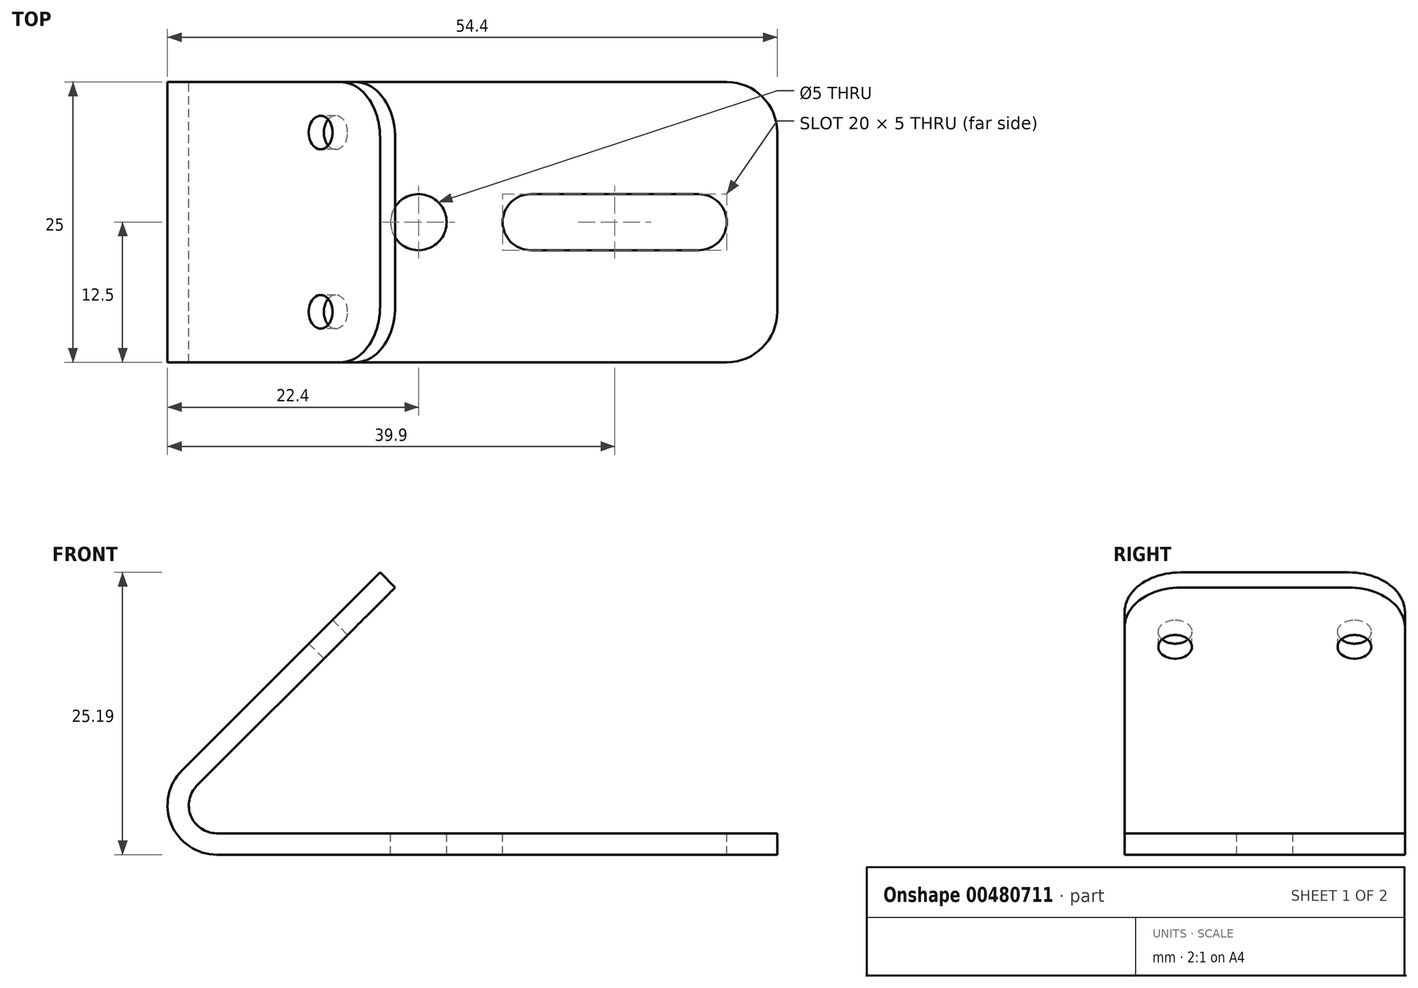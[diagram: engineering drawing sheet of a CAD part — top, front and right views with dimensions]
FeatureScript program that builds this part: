
annotation { "Feature Type Name" : "Feature", "Feature Type Description" : "" }
export const myFeature = defineFeature(function(context is Context, id is Id, definition is map)
    precondition{}
    {
        {
            var Q0;
            Q0=qCreatedBy(makeId("Front.planeOp"),FACE);
            var sketch = newSketch(context, id + "F0", { "sketchPlane" : qUnion([Q0])});
            skLineSegment(sketch, "E0", {"start": v(0, 0) * mm, "end": v(-50, 0) * mm});
            skLineSegment(sketch, "E1", {"start": v(-53.11, 7.51) * mm, "end": v(-35.43, 25.19) * mm});
            skPoint(sketch, "E2.visualSharp", {"position": v(-60.62, 0) * mm});
            skArc(sketch, "E2.filletArc", {"start": v(-53.11, 7.51) * mm, "mid": v(-54.07, 2.72) * mm, "end": v(-50, 0) * mm});
            skLineSegment(sketch, "E3.0", {"start": v(-51.77, 6.17) * mm, "end": v(-34.1, 23.85) * mm});
            skArc(sketch, "E3.1", {"start": v(-51.77, 6.17) * mm, "mid": v(-52.3, 3.44) * mm, "end": v(-50, 1.9) * mm});
            skLineSegment(sketch, "E3.2", {"start": v(0, 1.9) * mm, "end": v(-50, 1.9) * mm});
            skLineSegment(sketch, "E4", {"start": v(-35.43, 25.19) * mm, "end": v(-34.1, 23.85) * mm});
            skLineSegment(sketch, "E5", {"start": v(0, 1.9) * mm, "end": v(0, 0) * mm});
            skSolve(sketch);
        }
        {
            var Q0;
            Q0 = qSketchRegion(id + "F0", true);
            extrude(context, id + "F1", {"entities" : qUnion([Q0]), "endBound" : BoundingType.SYMMETRIC, "depth" : 25 * mm});
        }
        {
            var Q0;
            Q0=makeQuery(id+"F1.opExtrude","SWEPT_FACE",FACE,{"disambiguationData":[OSD([sQuery(id+"F0.wireOp",EDGE,"E3.2")])]});
            var sketch = newSketch(context, id + "F2", { "sketchPlane" : qUnion([Q0])});
            skCircle(sketch, "E6", {"center": v(-32, 0) * mm, "radius": 2.5 * mm});
            skLineSegment(sketch, "E7.0", {"start": v(-4.5, 12.5) * mm, "end": v(-50, 12.5) * mm});
            skLineSegment(sketch, "E8.0", {"start": v(0, -8) * mm, "end": v(0, 8) * mm});
            skLineSegment(sketch, "E9.0", {"start": v(-4.5, -12.5) * mm, "end": v(-50, -12.5) * mm});
            skPoint(sketch, "E10.visualSharp", {"position": v(0, 12.5) * mm});
            skArc(sketch, "E10.filletArc", {"start": v(0, 8) * mm, "mid": v(-1.32, 11.18) * mm, "end": v(-4.5, 12.5) * mm});
            skPoint(sketch, "E11.visualSharp", {"position": v(0, -12.5) * mm});
            skArc(sketch, "E11.filletArc", {"start": v(-4.5, -12.5) * mm, "mid": v(-1.32, -11.18) * mm, "end": v(0, -8) * mm});
            skLineSegment(sketch, "E12.bottom", {"start": v(-22, 2.5) * mm, "end": v(-7, 2.5) * mm});
            skLineSegment(sketch, "E12.top", {"start": v(-22, -2.5) * mm, "end": v(-7, -2.5) * mm});
            skPoint(sketch, "E12.middle", {"position": v(-14.5, 0) * mm});
            skArc(sketch, "E13", {"start": v(-22, 2.5) * mm, "mid": v(-24.5, 0) * mm, "end": v(-22, -2.5) * mm});
            skArc(sketch, "E14", {"start": v(-7, 2.5) * mm, "mid": v(-4.5, 0) * mm, "end": v(-7, -2.5) * mm});
            skSolve(sketch);
        }
        {
            var Q0;
            Q0=makeQuery(id+"F2.imprint","IMPRINT",FACE,{"disambiguationData":[TD([[makeQuery(id+"F2.imprint","IMPRINT",EDGE,{"derivedFrom":sQuery(id+"F2.wireOp",EDGE,"E6")}),1.0]])]});
            var Q1;
            {var subQ0=sQuery(id+"F2.wireOp",EDGE,"E10.filletArc");Q1=makeQuery(id+"F2.imprint","IMPRINT",FACE,{"disambiguationData":[TD([[makeQuery(id+"F2.imprint","IMPRINT",EDGE,{"derivedFrom":subQ0}),-1.0]])]});}
            var Q2;
            {var subQ0=sQuery(id+"F2.wireOp",EDGE,"E11.filletArc");Q2=makeQuery(id+"F2.imprint","IMPRINT",FACE,{"disambiguationData":[TD([[makeQuery(id+"F2.imprint","IMPRINT",EDGE,{"derivedFrom":subQ0}),-1.0]])]});}
            var Q3;
            Q3=makeQuery(id+"F2.imprint","IMPRINT",FACE,{"disambiguationData":[TD([[makeQuery(id+"F2.imprint","IMPRINT",EDGE,{"derivedFrom":sQuery(id+"F2.wireOp",EDGE,"E12.bottom")}),-1.0]])]});
            extrude(context, id + "F3", {"entities" : qUnion([Q0, Q1, Q2, Q3]), "operationType" : NewBodyOperationType.REMOVE, "endBound" : BoundingType.THROUGH_ALL, "oppositeDirection" : true, "depth" : 25 * mm});
        }
        {
            var Q0;
            Q0=makeQuery(id+"F1.opExtrude","SWEPT_FACE",FACE,{"disambiguationData":[OSD([sQuery(id+"F0.wireOp",EDGE,"E1")])]});
            var sketch = newSketch(context, id + "F4", { "sketchPlane" : qUnion([Q0])});
            skCircle(sketch, "E15", {"center": v(-8, -14.74) * mm, "radius": 1.5 * mm});
            skCircle(sketch, "E16", {"center": v(8, -14.74) * mm, "radius": 1.5 * mm});
            skLineSegment(sketch, "E17.0", {"start": v(12.5, -32.24) * mm, "end": v(12.5, -12.24) * mm});
            skLineSegment(sketch, "E18.0", {"start": v(-12.5, -32.24) * mm, "end": v(-12.5, -12.24) * mm});
            skLineSegment(sketch, "E19.0", {"start": v(7.5, -7.24) * mm, "end": v(-7.5, -7.24) * mm});
            skPoint(sketch, "E20.visualSharp", {"position": v(12.5, -7.24) * mm});
            skArc(sketch, "E20.filletArc", {"start": v(12.5, -12.24) * mm, "mid": v(11.04, -8.7) * mm, "end": v(7.5, -7.24) * mm});
            skPoint(sketch, "E21.visualSharp", {"position": v(-12.5, -7.24) * mm});
            skArc(sketch, "E21.filletArc", {"start": v(-7.5, -7.24) * mm, "mid": v(-11.04, -8.7) * mm, "end": v(-12.5, -12.24) * mm});
            skSolve(sketch);
        }
        {
            var Q0;
            Q0=makeQuery(id+"F4.imprint","IMPRINT",FACE,{"disambiguationData":[TD([[makeQuery(id+"F4.imprint","IMPRINT",EDGE,{"derivedFrom":sQuery(id+"F4.wireOp",EDGE,"E15")}),1.0]])]});
            var Q1;
            {var subQ0=sQuery(id+"F4.wireOp",EDGE,"E21.filletArc");Q1=makeQuery(id+"F4.imprint","IMPRINT",FACE,{"disambiguationData":[TD([[makeQuery(id+"F4.imprint","IMPRINT",EDGE,{"derivedFrom":subQ0}),-1.0]])]});}
            var Q2;
            Q2=makeQuery(id+"F4.imprint","IMPRINT",FACE,{"disambiguationData":[TD([[makeQuery(id+"F4.imprint","IMPRINT",EDGE,{"derivedFrom":sQuery(id+"F4.wireOp",EDGE,"E16")}),1.0]])]});
            var Q3;
            {var subQ0=sQuery(id+"F4.wireOp",EDGE,"E20.filletArc");Q3=makeQuery(id+"F4.imprint","IMPRINT",FACE,{"disambiguationData":[TD([[makeQuery(id+"F4.imprint","IMPRINT",EDGE,{"derivedFrom":subQ0}),-1.0]])]});}
            extrude(context, id + "F5", {"entities" : qUnion([Q0, Q1, Q2, Q3]), "operationType" : NewBodyOperationType.REMOVE, "endBound" : BoundingType.UP_TO_NEXT, "oppositeDirection" : true, "depth" : 25 * mm});
        }
    });
